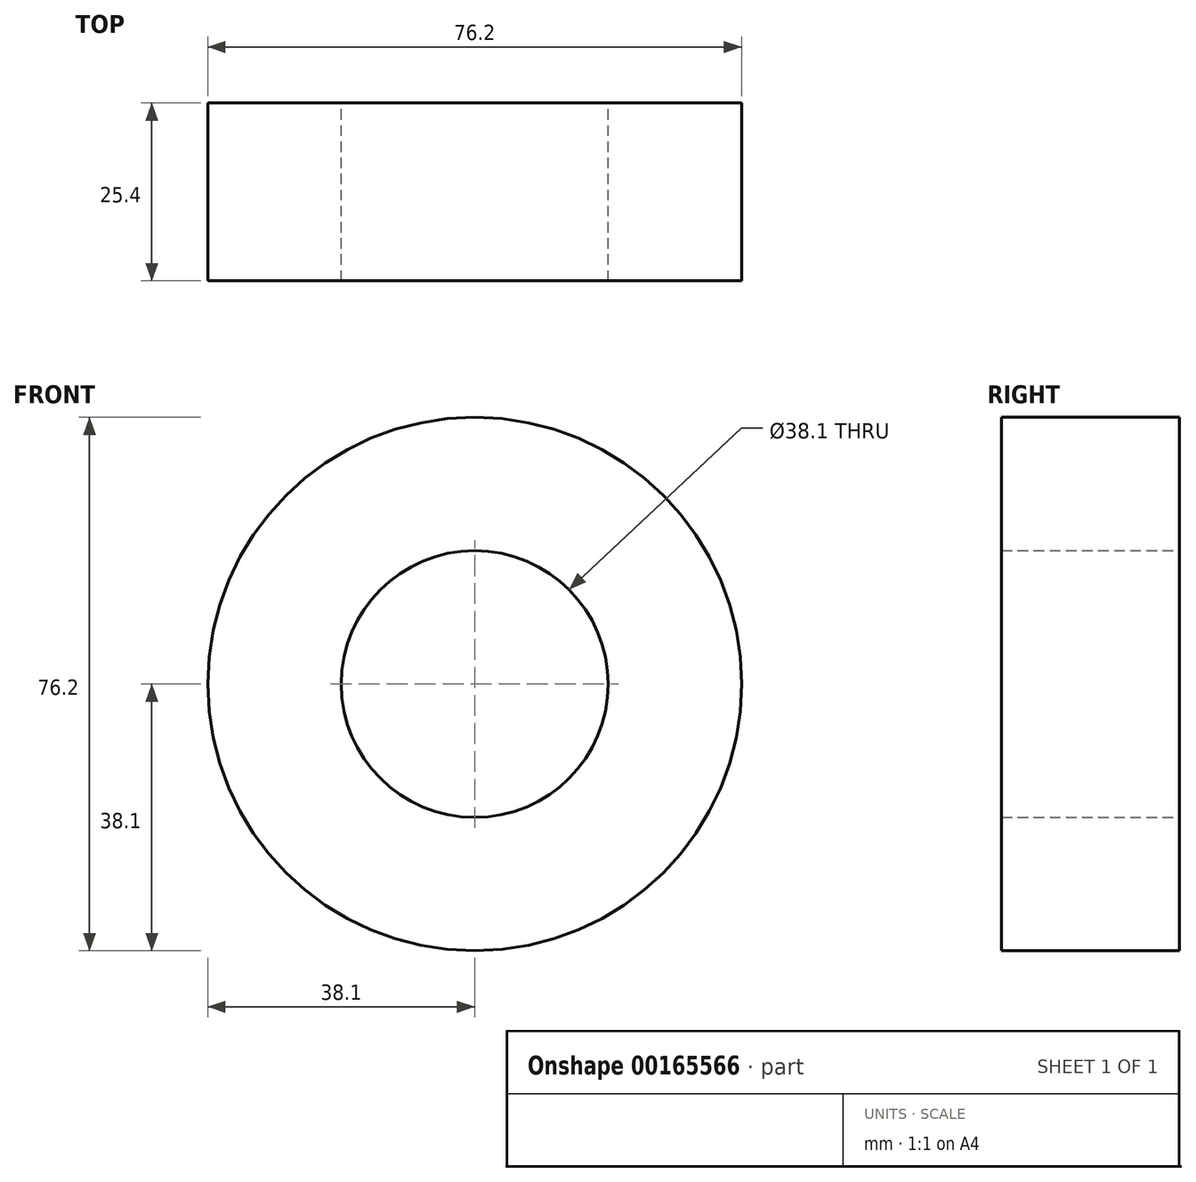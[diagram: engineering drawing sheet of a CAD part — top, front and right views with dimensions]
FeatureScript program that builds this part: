
annotation { "Feature Type Name" : "Feature", "Feature Type Description" : "" }
export const myFeature = defineFeature(function(context is Context, id is Id, definition is map)
    precondition{}
    {
        {
            var Q0;
            Q0=qCreatedBy(makeId("Front.planeOp"),FACE);
            var sketch = newSketch(context, id + "F0", { "sketchPlane" : qUnion([Q0])});
            skCircle(sketch, "E0", {"center": v(0, 0) * mm, "radius": 38.1 * mm});
            skCircle(sketch, "E1", {"center": v(0, 0) * mm, "radius": 19.05 * mm});
            skSolve(sketch);
        }
        {
            var Q0;
            Q0=makeQuery(id+"F0.imprint","IMPRINT",FACE,{"disambiguationData":[TD([[makeQuery(id+"F0.imprint","IMPRINT",EDGE,{"derivedFrom":sQuery(id+"F0.wireOp",EDGE,"E0")}),1.0]])]});
            extrude(context, id + "F1", {"entities" : qUnion([Q0]), "depth" : 25.4 * mm});
        }
    });
